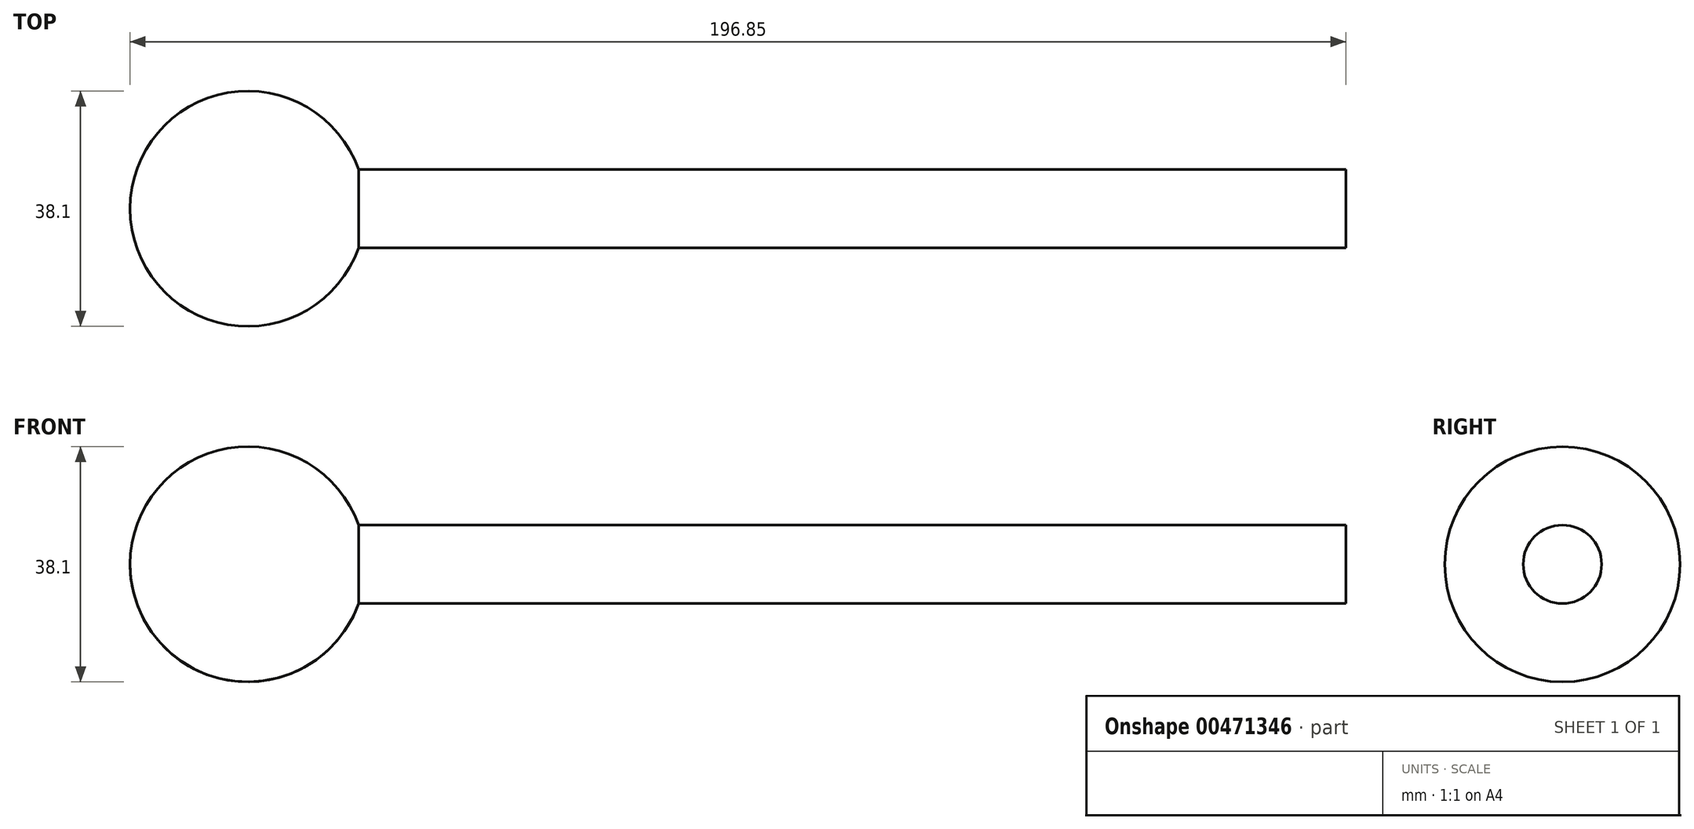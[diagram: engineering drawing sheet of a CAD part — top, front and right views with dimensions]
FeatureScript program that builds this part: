
annotation { "Feature Type Name" : "Feature", "Feature Type Description" : "" }
export const myFeature = defineFeature(function(context is Context, id is Id, definition is map)
    precondition{}
    {
        {
            var Q0;
            Q0=qCreatedBy(makeId("Front.planeOp"),FACE);
            var sketch = newSketch(context, id + "F0", { "sketchPlane" : qUnion([Q0])});
            skLineSegment(sketch, "E0.bottom", {"start": v(88.9, -6.35) * mm, "end": v(-88.9, -6.35) * mm});
            skLineSegment(sketch, "E0.top", {"start": v(88.9, 6.35) * mm, "end": v(-88.9, 6.35) * mm});
            skLineSegment(sketch, "E0.left", {"start": v(88.9, -6.35) * mm, "end": v(88.9, 6.35) * mm});
            skLineSegment(sketch, "E0.right", {"start": v(-88.9, -6.35) * mm, "end": v(-88.9, 6.35) * mm});
            skPoint(sketch, "E0.middle", {"position": v(0, 0) * mm});
            skLineSegment(sketch, "E1.0", {"start": v(88.9, 0) * mm, "end": v(-112.9, 0) * mm});
            skCircle(sketch, "E2", {"center": v(-88.9, 0) * mm, "radius": 19.05 * mm});
            skSolve(sketch);
        }
        {
            var Q0;
            {var subQ0=sQuery(id+"F0.wireOp",EDGE,"E0.right");var subQ1=sQuery(id+"F0.wireOp",EDGE,"E0.top");var subQ2=makeQuery(id+"F0.imprint","INTERSECT",VERTEX,{"derivedFrom":[subQ1,subQ0]});Q0=makeQuery(id+"F0.imprint","IMPRINT",FACE,{"disambiguationData":[TD([[makeQuery(id+"F0.imprint","IMPRINT",EDGE,{"disambiguationData":[TD([[subQ2,1.0]])],"derivedFrom":subQ1}),-1.0]])]});}
            var Q1;
            {var subQ0=sQuery(id+"F0.wireOp",EDGE,"E0.right");var subQ1=sQuery(id+"F0.wireOp",EDGE,"E0.top");var subQ2=makeQuery(id+"F0.imprint","INTERSECT",VERTEX,{"derivedFrom":[subQ1,subQ0]});Q1=makeQuery(id+"F0.imprint","IMPRINT",FACE,{"disambiguationData":[TD([[makeQuery(id+"F0.imprint","IMPRINT",EDGE,{"disambiguationData":[TD([[subQ2,1.0]])],"derivedFrom":subQ1}),1.0]])]});}
            var Q2;
            Q2=sQuery(id+"F0.wireOp",EDGE,"E1.0");
            revolve(context, id + "F1", {"entities" : qUnion([Q0, Q1]), "axis" : qUnion([Q2]), "revolveType" : RevolveType.FULL});
        }
        {
            var Q0;
            {var subQ0=sQuery(id+"F0.wireOp",EDGE,"E0.left");var subQ1=sQuery(id+"F0.wireOp",EDGE,"E0.top");var subQ2=makeQuery(id+"F0.imprint","INTERSECT",VERTEX,{"derivedFrom":[subQ1,subQ0]});Q0=makeQuery(id+"F0.imprint","IMPRINT",FACE,{"disambiguationData":[TD([[makeQuery(id+"F0.imprint","IMPRINT",EDGE,{"disambiguationData":[TD([[subQ2,-1.0]])],"derivedFrom":subQ1}),1.0]])]});}
            var Q1;
            Q1=sQuery(id+"F0.wireOp",EDGE,"E1.0");
            revolve(context, id + "F2", {"operationType" : NewBodyOperationType.ADD, "entities" : qUnion([Q0]), "axis" : qUnion([Q1]), "revolveType" : RevolveType.FULL});
        }
    });
